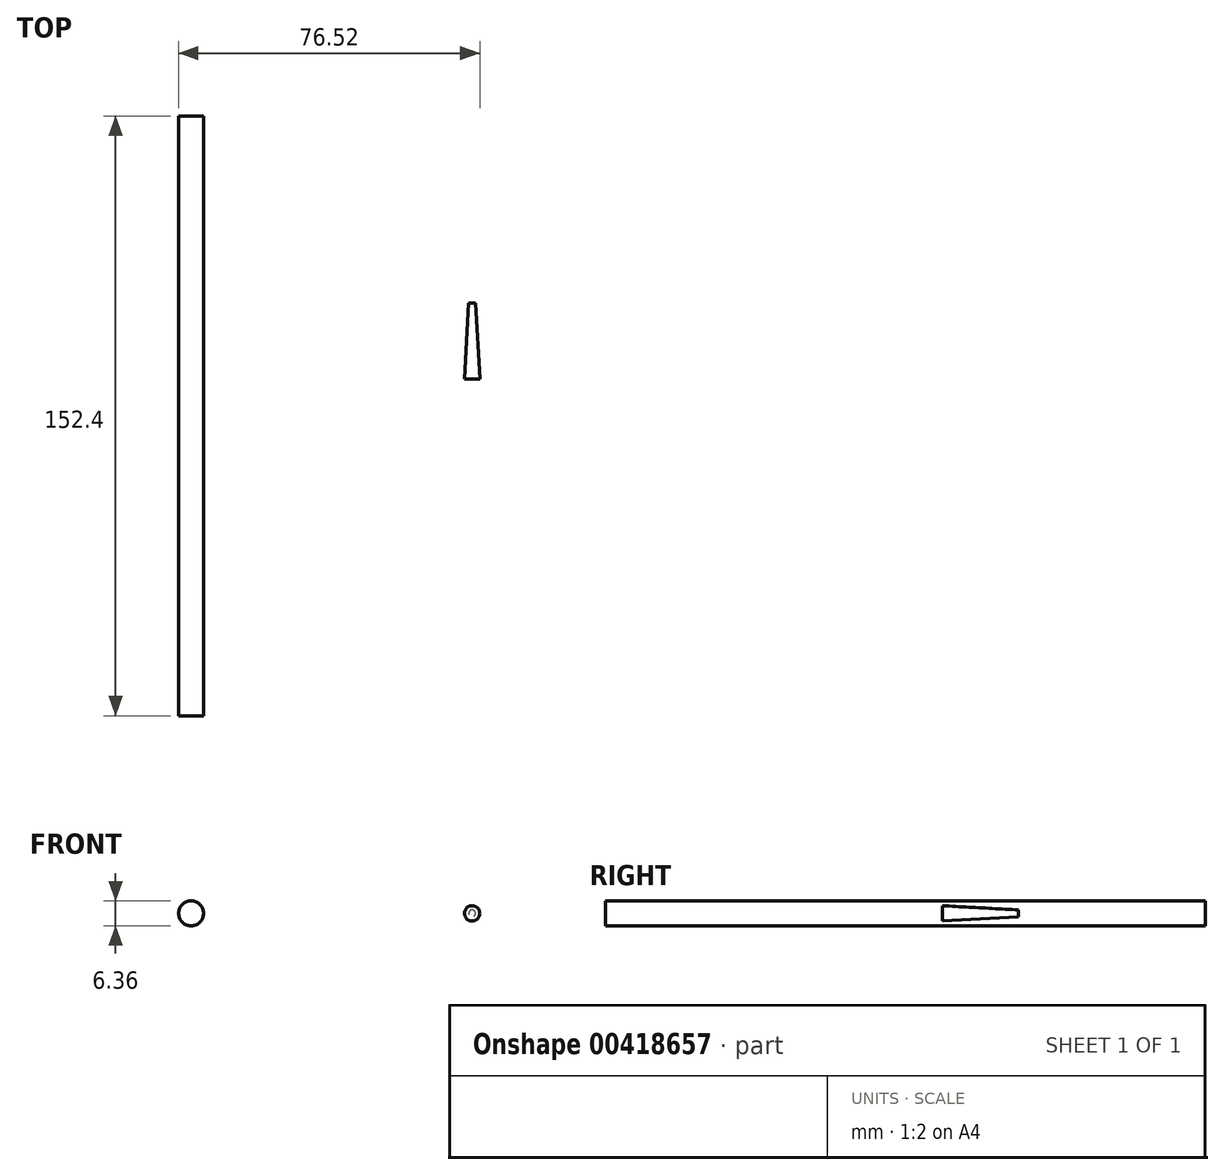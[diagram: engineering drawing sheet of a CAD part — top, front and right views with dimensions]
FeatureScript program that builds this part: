
annotation { "Feature Type Name" : "Feature", "Feature Type Description" : "" }
export const myFeature = defineFeature(function(context is Context, id is Id, definition is map)
    precondition{}
    {
        {
            var Q0;
            Q0=qCreatedBy(makeId("Top.planeOp"),FACE);
            var sketch = newSketch(context, id + "F0", { "sketchPlane" : qUnion([Q0])});
            skLineSegment(sketch, "E0", {"start": v(-51.08, 76.47) * mm, "end": v(-51.08, -75.93) * mm});
            skLineSegment(sketch, "E1", {"start": v(-51.08, 76.47) * mm, "end": v(-54.25, 76.47) * mm});
            skLineSegment(sketch, "E2", {"start": v(-54.25, -75.93) * mm, "end": v(-54.25, 76.47) * mm});
            skLineSegment(sketch, "E3", {"start": v(-54.25, -75.93) * mm, "end": v(-51.08, -75.93) * mm});
            skSolve(sketch);
        }
        {
            var Q0;
            Q0 = qSketchRegion(id + "F0", true);
            var Q1;
            Q1=sQuery(id+"F0.wireOp",EDGE,"E2");
            revolve(context, id + "F1", {"entities" : qUnion([Q0]), "axis" : qUnion([Q1]), "revolveType" : RevolveType.FULL});
        }
        {
            var Q0;
            Q0=qCreatedBy(makeId("Top.planeOp"),FACE);
            var sketch = newSketch(context, id + "F2", { "sketchPlane" : qUnion([Q0])});
            skLineSegment(sketch, "E4", {"start": v(17.15, 28.94) * mm, "end": v(17.15, 9.64) * mm});
            skLineSegment(sketch, "E5", {"start": v(17.15, 9.64) * mm, "end": v(19.09, 9.64) * mm});
            skLineSegment(sketch, "E6", {"start": v(19.09, 9.64) * mm, "end": v(18, 28.94) * mm});
            skLineSegment(sketch, "E7", {"start": v(17.15, 28.94) * mm, "end": v(18, 28.94) * mm});
            skSolve(sketch);
        }
        {
            var Q0;
            Q0 = qSketchRegion(id + "F2", true);
            var Q1;
            Q1=sQuery(id+"F2.wireOp",EDGE,"E4");
            revolve(context, id + "F3", {"entities" : qUnion([Q0]), "axis" : qUnion([Q1]), "revolveType" : RevolveType.FULL});
        }
    });
